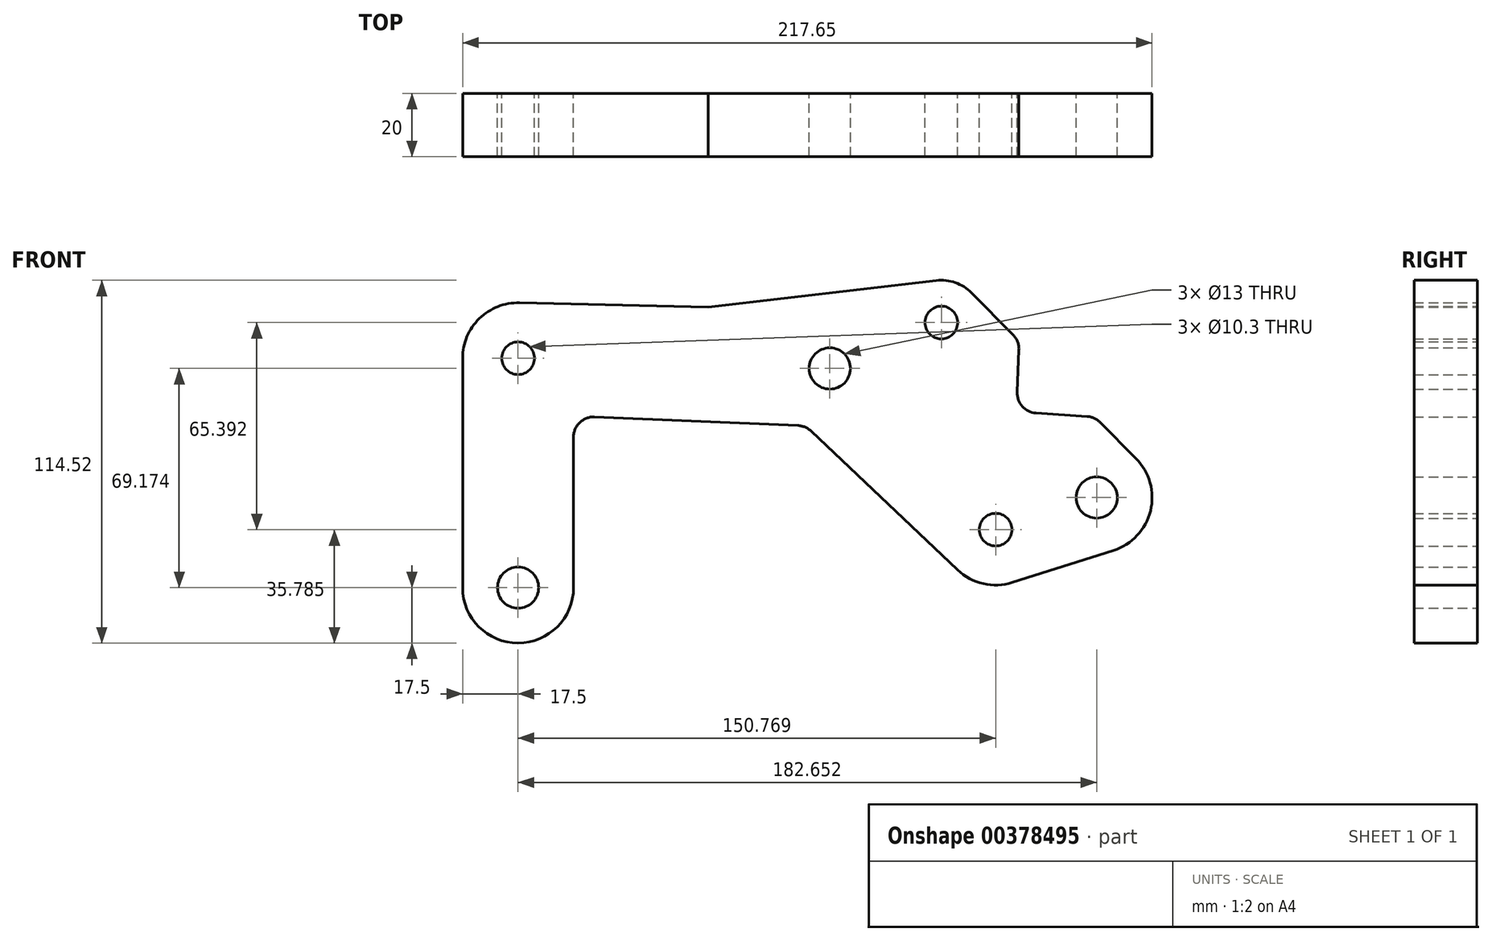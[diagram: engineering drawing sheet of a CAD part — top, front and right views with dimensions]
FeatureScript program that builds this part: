
annotation { "Feature Type Name" : "Feature", "Feature Type Description" : "" }
export const myFeature = defineFeature(function(context is Context, id is Id, definition is map)
    precondition{}
    {
        {
            var Q0;
            Q0=qCreatedBy(makeId("Front.planeOp"),FACE);
            var sketch = newSketch(context, id + "F0", { "sketchPlane" : qUnion([Q0])});
            skCircle(sketch, "E0", {"center": v(0, 0) * mm, "radius": 6.5 * mm});
            skCircle(sketch, "E1", {"center": v(0, 72.4) * mm, "radius": 5.1 * mm});
            skCircle(sketch, "E2", {"center": v(150.77, 18.28) * mm, "radius": 5.1 * mm});
            skCircle(sketch, "E3", {"center": v(182.65, 28.42) * mm, "radius": 6.5 * mm});
            skCircle(sketch, "E4", {"center": v(133.63, 83.68) * mm, "radius": 5.1 * mm});
            skCircle(sketch, "E5", {"center": v(0, 0) * mm, "radius": 17.5 * mm});
            skLineSegment(sketch, "E6", {"start": v(156.07, 1.6) * mm, "end": v(187.95, 11.74) * mm});
            skLineSegment(sketch, "E7", {"start": v(17.5, 47.53) * mm, "end": v(17.5, 0) * mm});
            skLineSegment(sketch, "E8", {"start": v(-17.5, 72.4) * mm, "end": v(-17.5, 0) * mm});
            skLineSegment(sketch, "E9", {"start": v(24.12, 53.87) * mm, "end": v(88.36, 51.15) * mm});
            skLineSegment(sketch, "E10", {"start": v(92.46, 49.41) * mm, "end": v(138.73, 5.58) * mm});
            skLineSegment(sketch, "E11", {"start": v(195.07, 40.75) * mm, "end": v(183.7, 52.2) * mm});
            skArc(sketch, "E12.filletArc", {"start": v(24.12, 53.87) * mm, "mid": v(19.46, 52.11) * mm, "end": v(17.5, 47.53) * mm});
            skArc(sketch, "E13.filletArc", {"start": v(92.46, 49.41) * mm, "mid": v(90.57, 50.65) * mm, "end": v(88.36, 51.15) * mm});
            skArc(sketch, "E14.filletArc", {"start": v(138.73, 5.58) * mm, "mid": v(146.86, 1.23) * mm, "end": v(156.07, 1.6) * mm});
            skArc(sketch, "E15.filletArc", {"start": v(187.95, 11.74) * mm, "mid": v(199.65, 24.25) * mm, "end": v(195.07, 40.75) * mm});
            skLineSegment(sketch, "E16", {"start": v(158.12, 75.07) * mm, "end": v(157.56, 61.69) * mm});
            skLineSegment(sketch, "E17", {"start": v(179.61, 54.05) * mm, "end": v(163.5, 55.09) * mm});
            skArc(sketch, "E18.filletArc", {"start": v(157.56, 61.69) * mm, "mid": v(159.19, 57.18) * mm, "end": v(163.5, 55.09) * mm});
            skLineSegment(sketch, "E19.trimOffspring", {"start": v(156.28, 79.8) * mm, "end": v(143.1, 93.08) * mm});
            skArc(sketch, "E20.filletArc", {"start": v(183.7, 52.2) * mm, "mid": v(181.83, 53.5) * mm, "end": v(179.61, 54.05) * mm});
            skArc(sketch, "E21.filletArc", {"start": v(158.12, 75.07) * mm, "mid": v(157.7, 77.63) * mm, "end": v(156.28, 79.8) * mm});
            skLineSegment(sketch, "E22", {"start": v(133.63, 83.68) * mm, "end": v(60.88, 77.54) * mm});
            skLineSegment(sketch, "E23", {"start": v(60.88, 77.54) * mm, "end": v(59.96, 88.53) * mm});
            skLineSegment(sketch, "E24", {"start": v(0.4, 89.9) * mm, "end": v(59.96, 88.53) * mm});
            skLineSegment(sketch, "E25", {"start": v(59.96, 88.53) * mm, "end": v(132.08, 96.93) * mm});
            skArc(sketch, "E26.filletArc", {"start": v(0.4, 89.9) * mm, "mid": v(-12.23, 84.93) * mm, "end": v(-17.5, 72.4) * mm});
            skArc(sketch, "E27.filletArc", {"start": v(143.1, 93.08) * mm, "mid": v(138.03, 96.28) * mm, "end": v(132.08, 96.93) * mm});
            skPoint(sketch, "E28", {"position": v(98.4, 69.17) * mm});
            skCircle(sketch, "E29", {"center": v(98.4, 69.17) * mm, "radius": 6.5 * mm});
            skSolve(sketch);
        }
        {
            var Q0;
            Q0 = qSketchRegion(id + "F0", true);
            var Q1;
            Q1=makeQuery(id+"F0.imprint","IMPRINT",FACE,{"disambiguationData":[TD([[makeQuery(id+"F0.imprint","IMPRINT",EDGE,{"derivedFrom":sQuery(id+"F0.wireOp",EDGE,"E4")}),1.0]])]});
            var Q2;
            Q2=makeQuery(id+"F0.imprint","IMPRINT",FACE,{"disambiguationData":[TD([[makeQuery(id+"F0.imprint","IMPRINT",EDGE,{"derivedFrom":sQuery(id+"F0.wireOp",EDGE,"E2")}),1.0]])]});
            var Q3;
            Q3=makeQuery(id+"F0.imprint","IMPRINT",FACE,{"disambiguationData":[TD([[makeQuery(id+"F0.imprint","IMPRINT",EDGE,{"derivedFrom":sQuery(id+"F0.wireOp",EDGE,"E1")}),1.0]])]});
            extrude(context, id + "F1", {"entities" : qUnion([Q0, Q1, Q2, Q3]), "depth" : 20 * mm});
        }
        {
            var Q0;
            Q0=sQuery(id+"F0.wireOp",VERTEX,"E1.center");
            var Q1;
            Q1=sQuery(id+"F0.wireOp",VERTEX,"E2.center");
            var Q2;
            Q2=sQuery(id+"F0.wireOp",VERTEX,"E4.center");
            var Q3;
            Q3=makeQuery(id+"F1.opExtrude","SWEPT_BODY",BODY,{"disambiguationData":[OSD([sQuery(id+"F0.wireOp",EDGE,"E0"),sQuery(id+"F0.wireOp",EDGE,"cMuSzexg-Rbci-06oe-gReg-Arz7SU72Ltpd"),sQuery(id+"F0.wireOp",EDGE,"E3"),sQuery(id+"F0.wireOp",EDGE,"E5"),sQuery(id+"F0.wireOp",EDGE,"E6"),sQuery(id+"F0.wireOp",EDGE,"E7"),sQuery(id+"F0.wireOp",EDGE,"E8"),sQuery(id+"F0.wireOp",EDGE,"E9"),sQuery(id+"F0.wireOp",EDGE,"E10"),sQuery(id+"F0.wireOp",EDGE,"E11"),sQuery(id+"F0.wireOp",EDGE,"E12.filletArc"),sQuery(id+"F0.wireOp",EDGE,"E13.filletArc"),sQuery(id+"F0.wireOp",EDGE,"E14.filletArc"),sQuery(id+"F0.wireOp",EDGE,"E15.filletArc"),sQuery(id+"F0.wireOp",EDGE,"E16"),sQuery(id+"F0.wireOp",EDGE,"E17"),sQuery(id+"F0.wireOp",EDGE,"E18.filletArc"),sQuery(id+"F0.wireOp",EDGE,"E19.trimOffspring"),sQuery(id+"F0.wireOp",EDGE,"E20.filletArc"),sQuery(id+"F0.wireOp",EDGE,"E21.filletArc"),sQuery(id+"F0.wireOp",EDGE,"E24"),sQuery(id+"F0.wireOp",EDGE,"E25"),sQuery(id+"F0.wireOp",EDGE,"E26.filletArc"),sQuery(id+"F0.wireOp",EDGE,"E27.filletArc")])]});
            hole(context, id + "F2", {"style" : HoleStyle.SIMPLE, "endStyle" : HoleEndStyle.THROUGH, "oppositeDirection" : true, "standardTappedOrClearance" : lookupTablePath({ "standard" : "ISO", "engagement" : "75%", "pitch" : "1.75 mm", "size" : "M12", "type" : "Tapped" }), "standardBlindInLast" : lookupTablePath({ "standard" : "ISO", "engagement" : "75%", "pitch" : "1.75 mm", "size" : "M12", "type" : "Tapped" }), "holeDiameter" : 10.3 * mm, "showTappedDepth" : true, "isTappedThrough" : true, "tappedDepth" : 17.25 * mm, "tapClearance" : 0, "locations" : qUnion([Q0, Q1, Q2]), "scope" : qUnion([Q3]), "majorDiameter" : 12 * mm});
        }
    });
